# Revit family: QF_ELECTROLUXPROFESSIONAL_1LSNTB_WS6-8_E
name_source: partatom
category: Attrezzature speciali
units: mm (PartAtom-declared; Revit-internal decimal feet)

## family parameters
Basato su piano di lavoro = No
Condiviso = No
Punto di calcolo locali = No
Quota connettore circolare = Usa diametro
Sempre verticale = Sì
Taglio con vuoti quando caricato = No
Tipo di parte = Normale

## types (12) — shared parameters
Depth = 682.4 mm  [stored 2.23885 ft]
Depth Actual = 680 mm  [stored 2.23097 ft]
Height = 1134.3 mm  [stored 3.72146 ft]
Height Actual = 1135 mm  [stored 3.72375 ft]
Latent Heat Output = 0.0
Length Actual = 660 mm  [stored 2.16535 ft]
Modello = WS6-8
Produttore = Electrolux Professional
Sensible Heat Output = 0.0
URL = www.electroluxprofessional.com
Weight = 116
Width = 660 mm  [stored 2.16535 ft]
zero-valued in all types: Gas KW, Prospetto di default, Steam Pounds per Hour

## per-type parameters (varying)
| type | Cycle | Descrizione | Item Number | Phase | Volts | Watts |
| 9867630225 | 50 Hz | WASHER WS6-8 8KG LE 3KW 380-415/50/3N COMPASS PRO 6A01 SE 2xWATER POWDER VALV.OPEN SILVER | 1L0GJ8 | 3 | 415 V | 3300 W |
| 9867630227 | 50 Hz | WASHER WS6-8 8KG NO HEAT 220-240/50/1N COMPASS PRO 6L01 ML 2xWATER POWDER+5xLIQ. VALV.OPEN SILVER ELS-NETW. 2.I/O DISCON | 1L0GJP | 1 | 240 V | 400 W |
| 9867630260 | 60 Hz | WASHER WS6-8 8KG EL 7,5KW 220-240/60/3 COMPASS PRO 6G01 ML 2xWATER POWDER+5xLIQ. VALV.OPEN SILVER 2.I/O DISCON. STOP | 1LSPG6 | 3 | 240 V | 7900 W |
| 9867630172 | 50 Hz | WASHER WS6-8 8KG MOP 7,5KW 380-415/50/3N COMPASS PRO 6F01 ML 2xWATER POWDER+ED EL.VALV.OPEN SST DISCON. STOP LID | 1L0GCR | 3 | 415 V | 7800 W |
| 9867630220 | 60 Hz | WASHER WS6-8 8KG EL 5,4KW 220-240/60/1N COMPASS PRO 6G07 ML 2xWATER POWDER+5xLIQ. VALV.OPEN SST/SILVER 2.I/O DISCON. STO | 1LSPC7 | 1 | 240 V | 5700 W |
| 9867630324 | 50 Hz | WASHER WS6-8 8KG MOP 7,5KW 380-415/220-240/50/3N/3 COMPASS PRO 6M14 ML 2xWATER POWDER+5xLIQ. EL.VALV.OPEN SILVER 2.I/O D | 1LT6F5 | 3 | 415 V | 7800 W |
| 9867630186 | 50 Hz | WASHER WS6-8 8KG NO HEAT 220-240/50/1N COMPASS PRO 6L01 ML 2xWATER POWDER+5xLIQ. VALV.OPEN SST/SILVER ELS-NETW. EXT.PM. | 1L0GDA | 1 | 240 V | 400 W |
| 9867630155 | 50 Hz | WASHER WS6-8 8KG EL 7,5KW 380-415/50/3N COMPASS PRO 6G01 ML 2xWATER POWDER+5xLIQ. VALV.OPEN SST/SILVER 2.I/O DISCON. STO | 1L821K | 3 | 415 V | 7800 W |
| 9867630231 | 60 Hz | WASHER WS6-8 8KG EL 7,5KW 440/60/3 COMPASS PRO 6G07 ML 2xWATER POWDER+5xLIQ. VALV.OPEN SILVER 2.I/O TRAFO DISCON. STOP | 1LA22L | 3 | 440 V | 7900 W |
| 9867630184 | 60 Hz | WASHER WS6-8 8KG NO HEAT 208-240/60/1 COMPASS PRO 6G01 ML 2xWATER POWDER+5xLIQ. VALV.CLOSED SILVER 2.I/O STOP | 1LSPA0 | 1 | 240 V | 400 W |
| 9867630208 | 50 Hz | WASHER WS6-8 8KG EL 5,4KW 380-415/50/3N COMPASS PRO 6G01 ML 2xWATER POWDER+5xLIQ. VALV.OPEN SILVER 2.I/O DISCON. STOP | 1LSPCH | 3 | 415 V | 3300 W |
| 9867630129 | 50 Hz | WASHER WS6-8 8KG NO HEAT 220-240/50/1N COMPASS PRO 6L01 ML 2xWATER POWDER+5xLIQ. VALV.OPEN SILVER EXT.PM. 2.I/O DISCON. | 1LSP3C | 1 | 240 V | 400 W |

note: [stored X ft] marks values corroborated as IEEE doubles in the binary element streams (Revit-internal decimal feet)

## geometry (parser evidence)
native form markers: Sweep x4
no freeform markers — native parametric forms only
